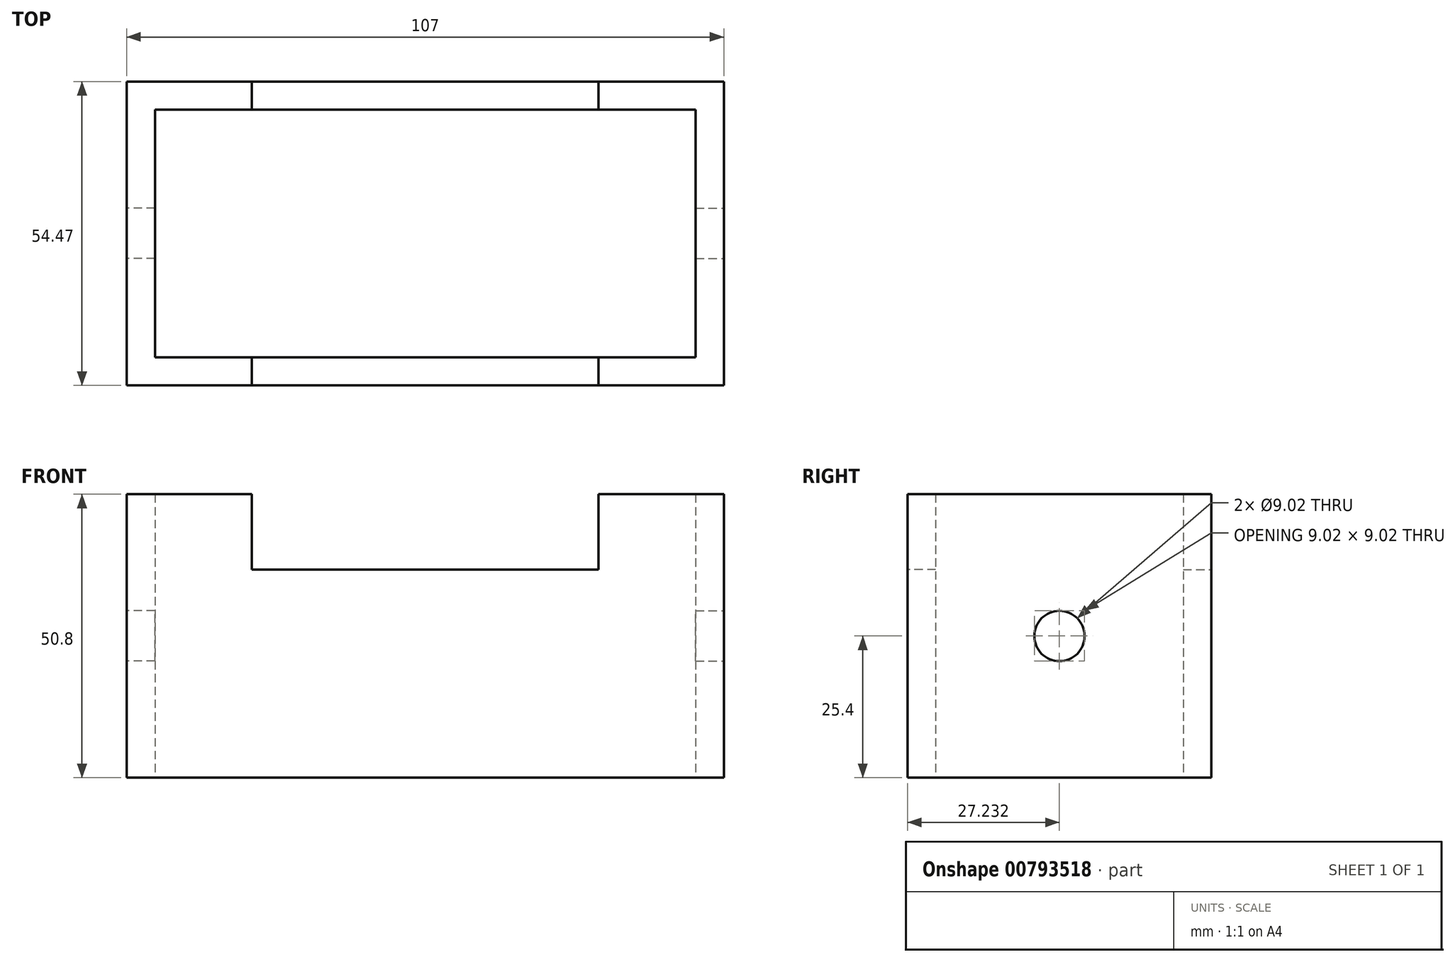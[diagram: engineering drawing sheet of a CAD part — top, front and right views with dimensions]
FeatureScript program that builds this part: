
annotation { "Feature Type Name" : "Feature", "Feature Type Description" : "" }
export const myFeature = defineFeature(function(context is Context, id is Id, definition is map)
    precondition{}
    {
        {
            var Q0;
            Q0=qCreatedBy(makeId("Top.planeOp"),FACE);
            var sketch = newSketch(context, id + "F0", { "sketchPlane" : qUnion([Q0])});
            skLineSegment(sketch, "E0", {"start": v(-67.12, 14.34) * mm, "end": v(-67.12, -12.9) * mm});
            skLineSegment(sketch, "E1", {"start": v(-67.12, -12.9) * mm, "end": v(-13.62, -12.9) * mm});
            skLineSegment(sketch, "E2", {"start": v(-13.62, -12.9) * mm, "end": v(-13.62, -7.83) * mm});
            skLineSegment(sketch, "E3", {"start": v(-13.62, -7.83) * mm, "end": v(-62.06, -7.83) * mm});
            skLineSegment(sketch, "E4", {"start": v(-62.06, 14.34) * mm, "end": v(-62.06, -7.83) * mm});
            skLineSegment(sketch, "E5", {"start": v(-62.06, 14.34) * mm, "end": v(-67.12, 14.34) * mm});
            skSolve(sketch);
        }
        {
            var Q0;
            Q0=makeQuery(id+"F0.imprint","IMPRINT",FACE,{"disambiguationData":[TD([[makeQuery(id+"F0.imprint","IMPRINT",EDGE,{"derivedFrom":sQuery(id+"F0.wireOp",EDGE,"E0")}),1.0]])]});
            extrude(context, id + "F1", {"entities" : qUnion([Q0]), "depth" : 50.8 * mm, "offsetDistance" : 25.4 * mm});
        }
        {
            var Q0;
            Q0=makeQuery(id+"F1.opExtrude","SWEPT_FACE",FACE,{"disambiguationData":[OSD([sQuery(id+"F0.wireOp",EDGE,"E1")])]});
            var sketch = newSketch(context, id + "F2", { "sketchPlane" : qUnion([Q0])});
            skLineSegment(sketch, "E6", {"start": v(-44.66, 50.8) * mm, "end": v(-44.66, 37.27) * mm});
            skLineSegment(sketch, "E7", {"start": v(-44.66, 37.27) * mm, "end": v(-13.62, 37.27) * mm});
            skSolve(sketch);
        }
        {
            var Q0;
            {var subQ0=sQuery(id+"F2.wireOp",EDGE,"E6");Q0=makeQuery(id+"F2.imprint","IMPRINT",FACE,{"disambiguationData":[TD([[makeQuery(id+"F2.imprint","IMPRINT",EDGE,{"derivedFrom":subQ0}),1.0]])]});}
            extrude(context, id + "F3", {"entities" : qUnion([Q0]), "operationType" : NewBodyOperationType.REMOVE, "oppositeDirection" : true, "depth" : 25.4 * mm, "offsetDistance" : 25.4 * mm});
        }
        {
            var Q0;
            Q0=makeQuery(id+"F1.opExtrude","SWEPT_FACE",FACE,{"disambiguationData":[OSD([sQuery(id+"F0.wireOp",EDGE,"E0")])]});
            var sketch = newSketch(context, id + "F4", { "sketchPlane" : qUnion([Q0])});
            skCircle(sketch, "E8", {"center": v(-14.34, 25.4) * mm, "radius": 4.5 * mm});
            skSolve(sketch);
        }
        {
            var Q0;
            {var subQ0=sQuery(id+"F4.wireOp",EDGE,"E8");var subQ1=makeQuery(id+"F1.opExtrude","SWEPT_EDGE",EDGE,{"disambiguationData":[OSD([sQuery(id+"F0.wireOp",EDGE,"E0"),sQuery(id+"F0.wireOp",EDGE,"E5")])]});var subQ2=makeQuery(id+"F4.imprint","INTERSECT",VERTEX,{"disambiguationData":[OD(0.0)],"derivedFrom":[subQ1,subQ0]});Q0=makeQuery(id+"F4.imprint","IMPRINT",FACE,{"disambiguationData":[TD([[makeQuery(id+"F4.imprint","IMPRINT",EDGE,{"disambiguationData":[TD([[subQ2,-1.0]])],"derivedFrom":subQ0}),1.0]])]});}
            extrude(context, id + "F5", {"entities" : qUnion([Q0]), "operationType" : NewBodyOperationType.REMOVE, "oppositeDirection" : true, "depth" : 25.4 * mm, "offsetDistance" : 25.4 * mm});
        }
        {
            var Q0;
            Q0=makeQuery(id+"F1.opExtrude","SWEPT_BODY",BODY,{"disambiguationData":[OSD([sQuery(id+"F0.wireOp",EDGE,"E0"),sQuery(id+"F0.wireOp",EDGE,"E1"),sQuery(id+"F0.wireOp",EDGE,"E2"),sQuery(id+"F0.wireOp",EDGE,"E3"),sQuery(id+"F0.wireOp",EDGE,"E4"),sQuery(id+"F0.wireOp",EDGE,"E5")])]});
            var Q1;
            {var subQ0=sQuery(id+"F0.wireOp",EDGE,"E0");var subQ1=sQuery(id+"F0.wireOp",EDGE,"E5");var subQ2=sQuery(id+"F0.wireOp",EDGE,"E4");Q1=makeQuery(id+"F5.boolean.opBoolean","SPLIT",FACE,{"disambiguationData":[TD([makeQuery(id+"F1.opExtrude","CAP_FACE",FACE,{"disambiguationData":[OSD([subQ0,sQuery(id+"F0.wireOp",EDGE,"E1"),sQuery(id+"F0.wireOp",EDGE,"E2"),sQuery(id+"F0.wireOp",EDGE,"E3"),subQ2,subQ1])],"isStart":true})])],"derivedFrom":makeQuery(id+"F1.opExtrude","SWEPT_FACE",FACE,{"disambiguationData":[OSD([subQ1])]})});}
            mirror(context, id + "F6", {"operationType" : NewBodyOperationType.ADD, "entities" : qUnion([Q0]), "mirrorPlane" : qUnion([Q1])});
        }
        {
            var Q0;
            Q0=makeQuery(id+"F1.opExtrude","SWEPT_BODY",BODY,{"disambiguationData":[OSD([sQuery(id+"F0.wireOp",EDGE,"E0"),sQuery(id+"F0.wireOp",EDGE,"E1"),sQuery(id+"F0.wireOp",EDGE,"E2"),sQuery(id+"F0.wireOp",EDGE,"E3"),sQuery(id+"F0.wireOp",EDGE,"E4"),sQuery(id+"F0.wireOp",EDGE,"E5")])]});
            var Q1;
            Q1=makeQuery(id+"F6.opPattern","COPY",FACE,{"derivedFrom":makeQuery(id+"F1.opExtrude","SWEPT_FACE",FACE,{"disambiguationData":[OSD([sQuery(id+"F0.wireOp",EDGE,"E2")])]}),"instanceName":"1"});
            mirror(context, id + "F7", {"operationType" : NewBodyOperationType.ADD, "entities" : qUnion([Q0]), "mirrorPlane" : qUnion([Q1])});
        }
    });
